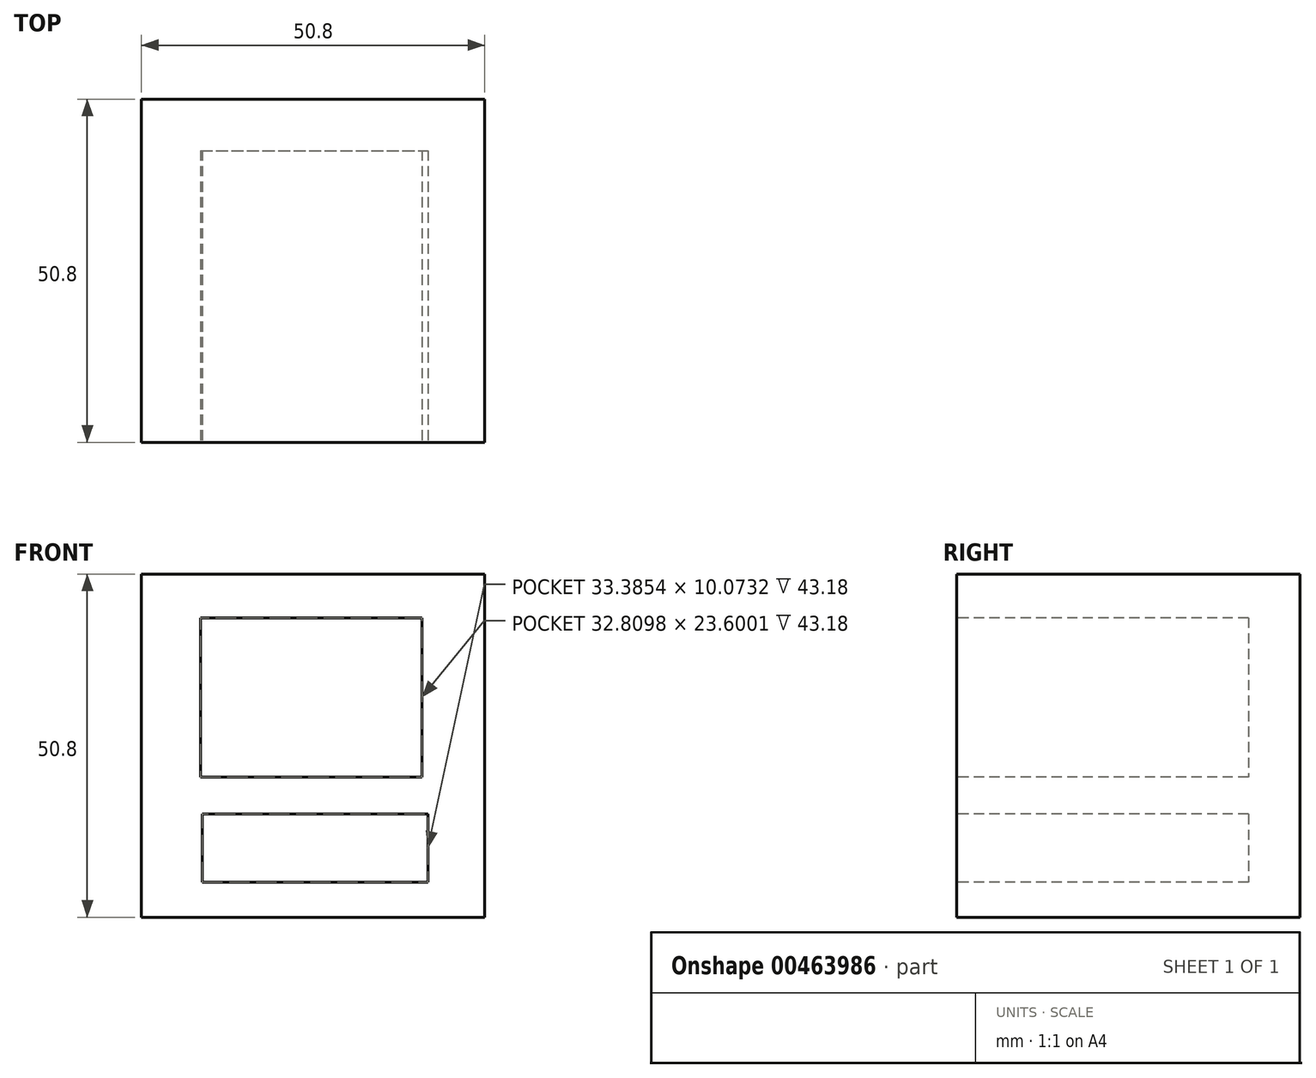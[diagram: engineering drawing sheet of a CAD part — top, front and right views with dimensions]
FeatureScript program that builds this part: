
annotation { "Feature Type Name" : "Feature", "Feature Type Description" : "" }
export const myFeature = defineFeature(function(context is Context, id is Id, definition is map)
    precondition{}
    {
        {
            var Q0;
            Q0=qCreatedBy(makeId("Top.planeOp"),FACE);
            var sketch = newSketch(context, id + "F0", { "sketchPlane" : qUnion([Q0])});
            skLineSegment(sketch, "E0.bottom", {"start": v(25.4, 25.4) * mm, "end": v(-25.4, 25.4) * mm});
            skLineSegment(sketch, "E0.top", {"start": v(25.4, -25.4) * mm, "end": v(-25.4, -25.4) * mm});
            skLineSegment(sketch, "E0.left", {"start": v(25.4, 25.4) * mm, "end": v(25.4, -25.4) * mm});
            skLineSegment(sketch, "E0.right", {"start": v(-25.4, 25.4) * mm, "end": v(-25.4, -25.4) * mm});
            skSolve(sketch);
        }
        {
            var Q0;
            Q0 = qSketchRegion(id + "F0", true);
            extrude(context, id + "F1", {"entities" : qUnion([Q0]), "depth" : 50.8 * mm});
        }
        {
            var Q0;
            Q0=makeQuery(id+"F1.opExtrude","SWEPT_FACE",FACE,{"disambiguationData":[OSD([sQuery(id+"F0.wireOp",EDGE,"E0.top")])]});
            var sketch = newSketch(context, id + "F2", { "sketchPlane" : qUnion([Q0])});
            skLineSegment(sketch, "E1.bottom", {"start": v(-16.7, 44.32) * mm, "end": v(16.12, 44.32) * mm});
            skLineSegment(sketch, "E1.top", {"start": v(-16.7, 20.72) * mm, "end": v(16.12, 20.72) * mm});
            skLineSegment(sketch, "E1.left", {"start": v(-16.7, 44.32) * mm, "end": v(-16.7, 20.72) * mm});
            skLineSegment(sketch, "E1.right", {"start": v(16.12, 44.32) * mm, "end": v(16.12, 20.72) * mm});
            skLineSegment(sketch, "E2.bottom", {"start": v(-16.4, 15.25) * mm, "end": v(16.98, 15.25) * mm});
            skLineSegment(sketch, "E2.top", {"start": v(-16.4, 5.18) * mm, "end": v(16.98, 5.18) * mm});
            skLineSegment(sketch, "E2.left", {"start": v(-16.4, 15.25) * mm, "end": v(-16.4, 5.18) * mm});
            skLineSegment(sketch, "E2.right", {"start": v(16.98, 15.25) * mm, "end": v(16.98, 5.18) * mm});
            skSolve(sketch);
        }
        {
            var Q0;
            Q0=makeQuery(id+"F2.imprint","IMPRINT",FACE,{"disambiguationData":[TD([[makeQuery(id+"F2.imprint","IMPRINT",EDGE,{"derivedFrom":sQuery(id+"F2.wireOp",EDGE,"E1.bottom")}),-1.0]])]});
            var Q1;
            Q1=makeQuery(id+"F2.imprint","IMPRINT",FACE,{"disambiguationData":[TD([[makeQuery(id+"F2.imprint","IMPRINT",EDGE,{"derivedFrom":sQuery(id+"F2.wireOp",EDGE,"E2.bottom")}),-1.0]])]});
            extrude(context, id + "F3", {"entities" : qUnion([Q0, Q1]), "operationType" : NewBodyOperationType.REMOVE, "depth" : -43.18 * mm});
        }
    });
